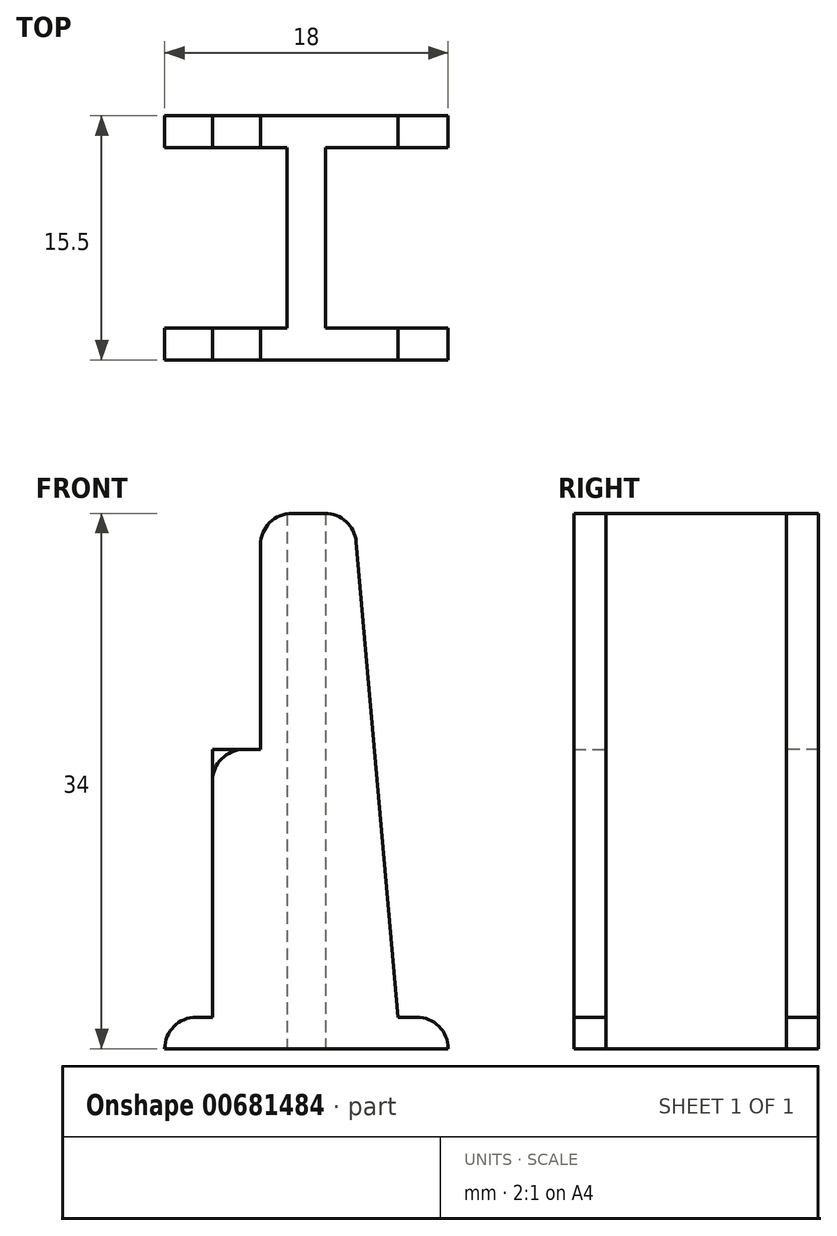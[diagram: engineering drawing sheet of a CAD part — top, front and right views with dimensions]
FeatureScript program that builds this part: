
annotation { "Feature Type Name" : "Feature", "Feature Type Description" : "" }
export const myFeature = defineFeature(function(context is Context, id is Id, definition is map)
    precondition{}
    {
        {
            var Q0;
            Q0=qCreatedBy(makeId("Top.planeOp"),FACE);
            var sketch = newSketch(context, id + "F0", { "sketchPlane" : qUnion([Q0])});
            skLineSegment(sketch, "E0.bottom", {"start": v(9, 7.75) * mm, "end": v(-9, 7.75) * mm});
            skLineSegment(sketch, "E0.left", {"start": v(9, 7.75) * mm, "end": v(9, -7.75) * mm});
            skPoint(sketch, "E0.middle", {"position": v(0, 0) * mm});
            skLineSegment(sketch, "E1.top", {"start": v(-9, 5.74) * mm, "end": v(-5.97, 5.74) * mm});
            skLineSegment(sketch, "E1.right", {"start": v(-5.97, 7.75) * mm, "end": v(-5.97, 5.74) * mm});
            skLineSegment(sketch, "E2.top", {"start": v(9, 5.73) * mm, "end": v(6, 5.73) * mm});
            skLineSegment(sketch, "E2.right", {"start": v(6, 7.75) * mm, "end": v(6, 5.73) * mm});
            skLineSegment(sketch, "E3.top", {"start": v(9, -5.73) * mm, "end": v(6, -5.73) * mm});
            skLineSegment(sketch, "E3.right", {"start": v(6, -7.75) * mm, "end": v(6, -5.73) * mm});
            skLineSegment(sketch, "E4.top", {"start": v(-9, -5.73) * mm, "end": v(-5.98, -5.73) * mm});
            skLineSegment(sketch, "E4.right", {"start": v(-5.98, -7.75) * mm, "end": v(-5.98, -5.73) * mm});
            skLineSegment(sketch, "E5.top", {"start": v(-5.98, -5.73) * mm, "end": v(-2.92, -5.73) * mm});
            skLineSegment(sketch, "E5.right", {"start": v(-2.92, -7.75) * mm, "end": v(-2.92, -5.73) * mm});
            skLineSegment(sketch, "E6.bottom", {"start": v(-5.97, 5.74) * mm, "end": v(-2.92, 5.74) * mm});
            skLineSegment(sketch, "E6.left", {"start": v(-5.97, 5.74) * mm, "end": v(-5.97, 7.75) * mm});
            skLineSegment(sketch, "E6.right", {"start": v(-2.92, 5.74) * mm, "end": v(-2.92, 7.75) * mm});
            skLineSegment(sketch, "E7.bottom", {"start": v(1.22, 7.5) * mm, "end": v(-1.22, 7.5) * mm});
            skLineSegment(sketch, "E7.top", {"start": v(1.22, -7.5) * mm, "end": v(-1.22, -7.5) * mm});
            skLineSegment(sketch, "E7.left", {"start": v(1.22, 7.5) * mm, "end": v(1.22, -7.5) * mm});
            skLineSegment(sketch, "E7.right", {"start": v(-1.22, 7.5) * mm, "end": v(-1.22, -7.5) * mm});
            skLineSegment(sketch, "E8", {"start": v(-2.92, 5.74) * mm, "end": v(-1.22, 5.74) * mm});
            skLineSegment(sketch, "E9", {"start": v(-2.92, -5.73) * mm, "end": v(-1.22, -5.73) * mm});
            skLineSegment(sketch, "E10", {"start": v(6, 5.73) * mm, "end": v(1.22, 5.73) * mm});
            skLineSegment(sketch, "E11", {"start": v(6, -5.73) * mm, "end": v(1.22, -5.73) * mm});
            skLineSegment(sketch, "E12", {"start": v(-9, 7.75) * mm, "end": v(-9, -7.75) * mm});
            skLineSegment(sketch, "E13", {"start": v(-9, -7.75) * mm, "end": v(9, -7.75) * mm});
            skSolve(sketch);
        }
        {
            var Q0;
            {var subQ4=sQuery(id+"F0.wireOp",EDGE,"E1.top");Q0=makeQuery(id+"F0.imprint","IMPRINT",FACE,{"disambiguationData":[TD([[makeQuery(id+"F0.imprint","IMPRINT",EDGE,{"derivedFrom":subQ4}),1.0]])]});}
            var Q1;
            {var subQ4=sQuery(id+"F0.wireOp",EDGE,"E2.top");Q1=makeQuery(id+"F0.imprint","IMPRINT",FACE,{"disambiguationData":[TD([[makeQuery(id+"F0.imprint","IMPRINT",EDGE,{"derivedFrom":subQ4}),-1.0]])]});}
            var Q2;
            {var subQ3=sQuery(id+"F0.wireOp",EDGE,"E3.top");Q2=makeQuery(id+"F0.imprint","IMPRINT",FACE,{"disambiguationData":[TD([[makeQuery(id+"F0.imprint","IMPRINT",EDGE,{"derivedFrom":subQ3}),1.0]])]});}
            var Q3;
            {var subQ0=sQuery(id+"F0.wireOp",EDGE,"E4.top");Q3=makeQuery(id+"F0.imprint","IMPRINT",FACE,{"disambiguationData":[TD([[makeQuery(id+"F0.imprint","IMPRINT",EDGE,{"derivedFrom":subQ0}),-1.0]])]});}
            extrude(context, id + "F1", {"entities" : qUnion([Q0, Q1, Q2, Q3]), "depth" : 2 * mm, "offsetDistance" : 25 * mm});
        }
        {
            var Q0;
            {var subQ3=sQuery(id+"F0.wireOp",EDGE,"E7.bottom");Q0=makeQuery(id+"F0.imprint","IMPRINT",FACE,{"disambiguationData":[TD([[makeQuery(id+"F0.imprint","IMPRINT",EDGE,{"derivedFrom":subQ3}),1.0]])]});}
            extrude(context, id + "F2", {"entities" : qUnion([Q0]), "operationType" : NewBodyOperationType.ADD, "depth" : 34 * mm, "offsetDistance" : 25 * mm});
        }
        {
            var Q0;
            {var subQ3=sQuery(id+"F0.wireOp",EDGE,"E2.right");Q0=makeQuery(id+"F0.imprint","IMPRINT",FACE,{"disambiguationData":[TD([[makeQuery(id+"F0.imprint","IMPRINT",EDGE,{"derivedFrom":subQ3}),-1.0]])]});}
            var Q1;
            {var subQ6=sQuery(id+"F0.wireOp",EDGE,"E3.right");Q1=makeQuery(id+"F0.imprint","IMPRINT",FACE,{"disambiguationData":[TD([[makeQuery(id+"F0.imprint","IMPRINT",EDGE,{"derivedFrom":subQ6}),1.0]])]});}
            extrude(context, id + "F3", {"entities" : qUnion([Q0, Q1]), "operationType" : NewBodyOperationType.ADD, "depth" : 34 * mm, "offsetDistance" : 25 * mm});
        }
        {
            var Q0;
            Q0=makeQuery(id+"F0.imprint","IMPRINT",FACE,{"disambiguationData":[TD([[makeQuery(id+"F0.imprint","IMPRINT",EDGE,{"derivedFrom":sQuery(id+"F0.wireOp",EDGE,"E5.top")}),-1.0]])]});
            var Q1;
            Q1=makeQuery(id+"F0.imprint","IMPRINT",FACE,{"disambiguationData":[TD([[makeQuery(id+"F0.imprint","IMPRINT",EDGE,{"derivedFrom":sQuery(id+"F0.wireOp",EDGE,"E6.bottom")}),1.0]])]});
            extrude(context, id + "F4", {"entities" : qUnion([Q0, Q1]), "operationType" : NewBodyOperationType.ADD, "depth" : 19 * mm, "offsetDistance" : 25 * mm});
        }
        {
            var Q0;
            Q0=makeQuery(id+"F3.opExtrude","CAP_EDGE",EDGE,{"disambiguationData":[OSD([sQuery(id+"F0.wireOp",EDGE,"E3.right")])],"isStart":false});
            chamfer(context, id + "F5", {"entities" : qUnion([Q0]), "chamferType" : ChamferType.TWO_OFFSETS, "width1" : 3 * mm, "oppositeDirection" : false, "width2" : 34 * mm, "tangentPropagation" : true});
        }
        {
            var Q0;
            Q0=makeQuery(id+"F3.opExtrude","CAP_EDGE",EDGE,{"disambiguationData":[OSD([sQuery(id+"F0.wireOp",EDGE,"E2.right")])],"isStart":false});
            chamfer(context, id + "F6", {"entities" : qUnion([Q0]), "chamferType" : ChamferType.TWO_OFFSETS, "width1" : 34 * mm, "oppositeDirection" : false, "width2" : 3 * mm, "tangentPropagation" : true});
        }
        {
            var Q0;
            Q0=makeQuery(id+"F3.opExtrude","CAP_EDGE",EDGE,{"disambiguationData":[OSD([sQuery(id+"F0.wireOp",EDGE,"E5.right")])],"isStart":false});
            var Q1;
            Q1=makeQuery(id+"F4.opExtrude","CAP_EDGE",EDGE,{"disambiguationData":[OSD([sQuery(id+"F0.wireOp",EDGE,"E4.right")])],"isStart":false});
            var Q2;
            Q2=makeQuery(id+"F4.opExtrude","CAP_EDGE",EDGE,{"disambiguationData":[OSD([sQuery(id+"F0.wireOp",EDGE,"E6.left")])],"isStart":false});
            var Q3;
            Q3=makeQuery(id+"F3.opExtrude","CAP_EDGE",EDGE,{"disambiguationData":[OSD([sQuery(id+"F0.wireOp",EDGE,"E6.right")])],"isStart":false});
            var Q4;
            {var subQ0=sQuery(id+"F0.wireOp",EDGE,"E12");Q4=makeQuery(id+"F1.opExtrude","CAP_EDGE",EDGE,{"disambiguationData":[OSD([subQ0]),TDD([makeQuery(id+"F0.imprint","IMPRINT",EDGE,{"disambiguationData":[TD([[makeQuery(id+"F0.imprint","INTERSECT",VERTEX,{"derivedFrom":[sQuery(id+"F0.wireOp",EDGE,"E0.bottom"),subQ0]}),-1.0]])],"derivedFrom":subQ0})])],"isStart":false});}
            var Q5;
            {var subQ0=sQuery(id+"F0.wireOp",EDGE,"E12");Q5=makeQuery(id+"F1.opExtrude","CAP_EDGE",EDGE,{"disambiguationData":[OSD([subQ0]),TDD([makeQuery(id+"F0.imprint","IMPRINT",EDGE,{"disambiguationData":[TD([[makeQuery(id+"F0.imprint","INTERSECT",VERTEX,{"derivedFrom":[sQuery(id+"F0.wireOp",EDGE,"E4.top"),subQ0]}),-1.0]])],"derivedFrom":subQ0})])],"isStart":false});}
            var Q6;
            {var subQ0=sQuery(id+"F0.wireOp",EDGE,"E0.left");Q6=makeQuery(id+"F1.opExtrude","CAP_EDGE",EDGE,{"disambiguationData":[OSD([subQ0]),TDD([makeQuery(id+"F0.imprint","IMPRINT",EDGE,{"disambiguationData":[TD([[makeQuery(id+"F0.imprint","INTERSECT",VERTEX,{"derivedFrom":[subQ0,sQuery(id+"F0.wireOp",EDGE,"E13")]}),1.0]])],"derivedFrom":subQ0})])],"isStart":false});}
            var Q7;
            {var subQ0=sQuery(id+"F0.wireOp",EDGE,"E0.left");Q7=makeQuery(id+"F1.opExtrude","CAP_EDGE",EDGE,{"disambiguationData":[OSD([subQ0]),TDD([makeQuery(id+"F0.imprint","IMPRINT",EDGE,{"disambiguationData":[TD([[makeQuery(id+"F0.imprint","INTERSECT",VERTEX,{"derivedFrom":[sQuery(id+"F0.wireOp",EDGE,"E0.bottom"),subQ0]}),-1.0]])],"derivedFrom":subQ0})])],"isStart":false});}
            fillet(context, id + "F7", {"entities" : qUnion([Q0, Q1, Q2, Q3, Q4, Q5, Q6, Q7]), "radius" : 2 * mm, "tangentPropagation" : true, "allowEdgeOverflow" : false});
        }
        {
            var Q0;
            {var subQ0=sQuery(id+"F0.wireOp",EDGE,"E7.right");var subQ1=sQuery(id+"F0.wireOp",EDGE,"E7.left");var subQ2=sQuery(id+"F0.wireOp",EDGE,"E7.top");var subQ3=sQuery(id+"F0.wireOp",EDGE,"E3.right");var subQ4=sQuery(id+"F0.wireOp",EDGE,"E7.bottom");Q0=makeQuery(id+"F5.opChamfer","BLEND_EDGE",EDGE,{"blendedFrom":[makeQuery(id+"F3.opExtrude","CAP_EDGE",EDGE,{"disambiguationData":[OSD([subQ3])],"isStart":false}),makeQuery(id+"F3.boolean.opBoolean","MERGE",FACE,{"derivedFrom":[makeQuery(id+"F2.opExtrude","CAP_FACE",FACE,{"disambiguationData":[OSD([subQ4,subQ2,subQ1,subQ0])],"isStart":false}),makeQuery(id+"F3.opExtrude","CAP_FACE",FACE,{"disambiguationData":[OSD([sQuery(id+"F0.wireOp",EDGE,"E0.bottom"),sQuery(id+"F0.wireOp",EDGE,"E2.right"),sQuery(id+"F0.wireOp",EDGE,"E6.right"),subQ4,subQ1,subQ0,sQuery(id+"F0.wireOp",EDGE,"E8"),sQuery(id+"F0.wireOp",EDGE,"E10")])],"isStart":false}),makeQuery(id+"F3.opExtrude","CAP_FACE",FACE,{"disambiguationData":[OSD([subQ3,sQuery(id+"F0.wireOp",EDGE,"E5.right"),subQ2,subQ1,subQ0,sQuery(id+"F0.wireOp",EDGE,"E9"),sQuery(id+"F0.wireOp",EDGE,"E11"),sQuery(id+"F0.wireOp",EDGE,"E13")])],"isStart":false})]})],"blendedInto":[makeQuery(id+"F3.boolean.opBoolean","MERGE",FACE,{"derivedFrom":[makeQuery(id+"F2.opExtrude","CAP_FACE",FACE,{"disambiguationData":[OSD([subQ4,subQ2,subQ1,subQ0])],"isStart":false}),makeQuery(id+"F3.opExtrude","CAP_FACE",FACE,{"disambiguationData":[OSD([sQuery(id+"F0.wireOp",EDGE,"E0.bottom"),sQuery(id+"F0.wireOp",EDGE,"E2.right"),sQuery(id+"F0.wireOp",EDGE,"E6.right"),subQ4,subQ1,subQ0,sQuery(id+"F0.wireOp",EDGE,"E8"),sQuery(id+"F0.wireOp",EDGE,"E10")])],"isStart":false}),makeQuery(id+"F3.opExtrude","CAP_FACE",FACE,{"disambiguationData":[OSD([subQ3,sQuery(id+"F0.wireOp",EDGE,"E5.right"),subQ2,subQ1,subQ0,sQuery(id+"F0.wireOp",EDGE,"E9"),sQuery(id+"F0.wireOp",EDGE,"E11"),sQuery(id+"F0.wireOp",EDGE,"E13")])],"isStart":false})]})]});}
            fillet(context, id + "F8", {"entities" : qUnion([Q0]), "radius" : 2 * mm, "tangentPropagation" : true, "allowEdgeOverflow" : false});
        }
    });
